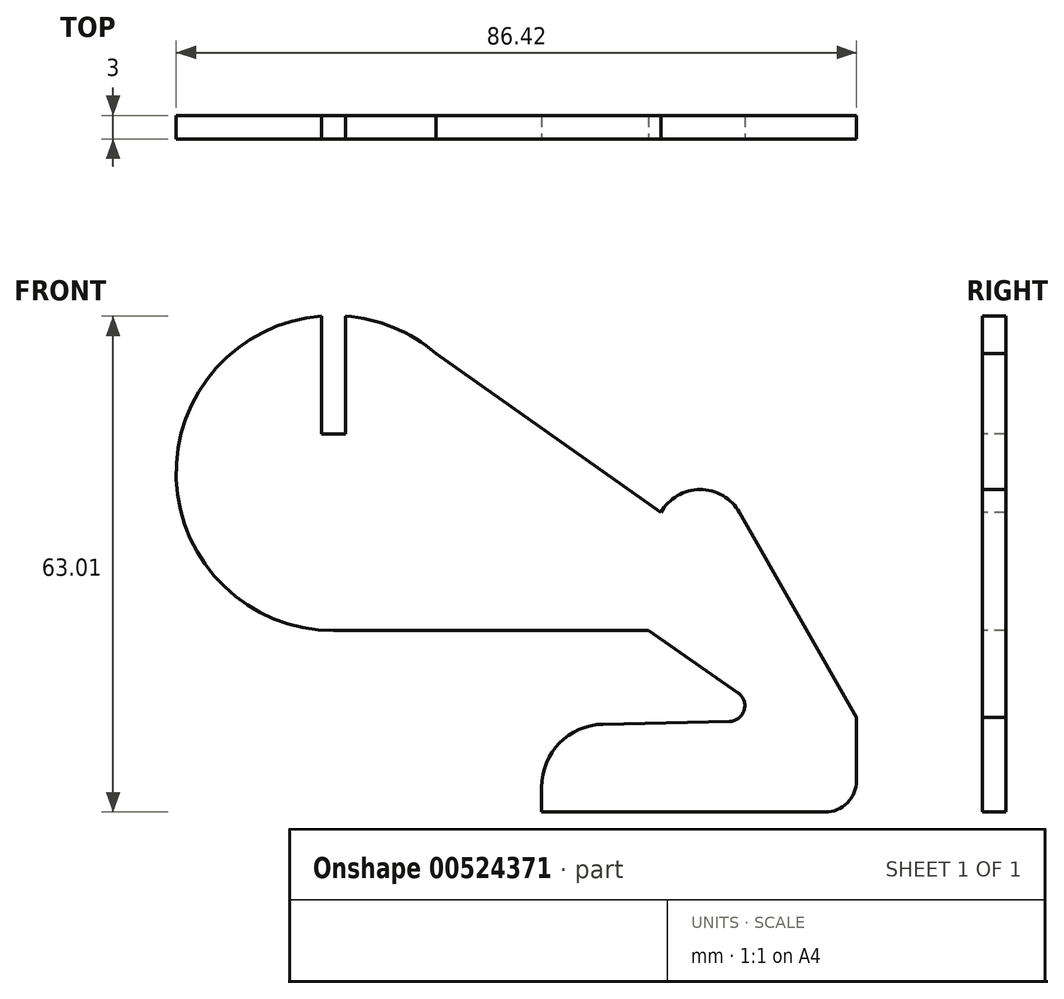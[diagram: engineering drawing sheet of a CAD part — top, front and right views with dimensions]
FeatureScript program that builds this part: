
annotation { "Feature Type Name" : "Feature", "Feature Type Description" : "" }
export const myFeature = defineFeature(function(context is Context, id is Id, definition is map)
    precondition{}
    {
        {
            var Q0;
            Q0=qCreatedBy(makeId("Front.planeOp"),FACE);
            var sketch = newSketch(context, id + "F0", { "sketchPlane" : qUnion([Q0])});
            skArc(sketch, "E0", {"start": v(-45.22, 49.44) * mm, "mid": v(-63.7, 28.75) * mm, "end": v(-43.72, 9.5) * mm});
            skLineSegment(sketch, "E1", {"start": v(-45.22, 49.44) * mm, "end": v(-45.22, 34.44) * mm});
            skLineSegment(sketch, "E2", {"start": v(-45.22, 34.44) * mm, "end": v(-42.22, 34.44) * mm});
            skLineSegment(sketch, "E3", {"start": v(-42.22, 34.44) * mm, "end": v(-42.22, 49.44) * mm});
            skLineSegment(sketch, "E4", {"start": v(-43.72, 9.5) * mm, "end": v(-3.72, 9.5) * mm});
            skLineSegment(sketch, "E5", {"start": v(-30.73, 44.7) * mm, "end": v(-2.16, 24.5) * mm});
            skArc(sketch, "E6", {"start": v(7.84, 24.5) * mm, "mid": v(2.84, 27.4) * mm, "end": v(-2.16, 24.5) * mm});
            skLineSegment(sketch, "E7", {"start": v(7.84, 24.5) * mm, "end": v(22.7, -1.57) * mm});
            skLineSegment(sketch, "E8", {"start": v(-3.72, 9.5) * mm, "end": v(7.65, 1.58) * mm});
            skLineSegment(sketch, "E9", {"start": v(22.7, -1.57) * mm, "end": v(22.7, -9.57) * mm});
            skLineSegment(sketch, "E10", {"start": v(18.7, -13.57) * mm, "end": v(-17.3, -13.57) * mm});
            skLineSegment(sketch, "E11", {"start": v(-17.3, -13.57) * mm, "end": v(-17.3, -10.4) * mm});
            skLineSegment(sketch, "E12", {"start": v(-9.47, -2.4) * mm, "end": v(6.56, -2.06) * mm});
            skPoint(sketch, "E13.visualSharp", {"position": v(12.7, -1.93) * mm});
            skArc(sketch, "E13.filletArc", {"start": v(6.56, -2.06) * mm, "mid": v(8.43, -0.64) * mm, "end": v(7.65, 1.58) * mm});
            skPoint(sketch, "E14.visualSharp", {"position": v(-17.3, -2.57) * mm});
            skArc(sketch, "E14.filletArc", {"start": v(-9.47, -2.4) * mm, "mid": v(-15.02, -4.8) * mm, "end": v(-17.3, -10.4) * mm});
            skPoint(sketch, "E15.visualSharp", {"position": v(22.7, -13.57) * mm});
            skArc(sketch, "E15.filletArc", {"start": v(18.7, -13.57) * mm, "mid": v(21.53, -12.4) * mm, "end": v(22.7, -9.57) * mm});
            skArc(sketch, "E16.trimOffspring", {"start": v(-30.73, 44.7) * mm, "mid": v(-36.1, 47.99) * mm, "end": v(-42.22, 49.44) * mm});
            skSolve(sketch);
        }
        {
            var Q0;
            Q0=makeQuery(id+"F0.imprint","IMPRINT",FACE,{"disambiguationData":[TD([[makeQuery(id+"F0.imprint","IMPRINT",EDGE,{"derivedFrom":sQuery(id+"F0.wireOp",EDGE,"E0")}),1.0]])]});
            extrude(context, id + "F1", {"entities" : qUnion([Q0]), "oppositeDirection" : true, "depth" : 3 * mm, "offsetDistance" : 25 * mm});
        }
    });
